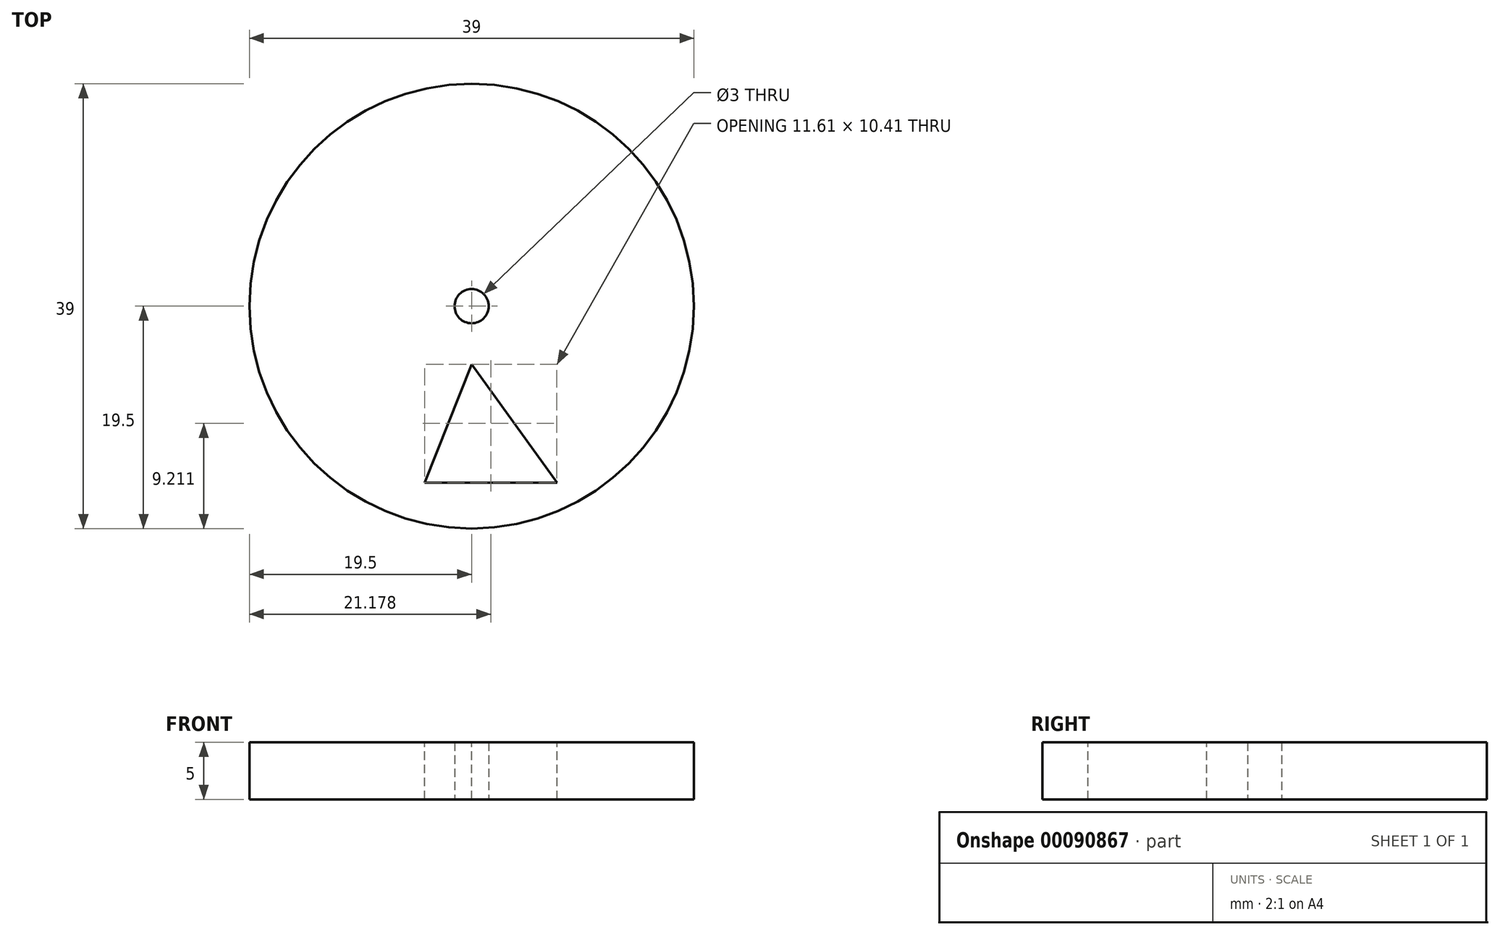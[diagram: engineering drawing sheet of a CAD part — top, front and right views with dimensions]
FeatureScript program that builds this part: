
annotation { "Feature Type Name" : "Feature", "Feature Type Description" : "" }
export const myFeature = defineFeature(function(context is Context, id is Id, definition is map)
    precondition{}
    {
        {
            var Q0;
            Q0=qCreatedBy(makeId("Top.planeOp"),FACE);
            var sketch = newSketch(context, id + "F0", { "sketchPlane" : qUnion([Q0])});
            skCircle(sketch, "E0", {"center": v(0, 0) * mm, "radius": 19.5 * mm});
            skCircle(sketch, "E1", {"center": v(0, 0) * mm, "radius": 1.5 * mm});
            skSolve(sketch);
        }
        {
            var Q0;
            Q0=makeQuery(id+"F0.imprint","IMPRINT",FACE,{"disambiguationData":[TD([[makeQuery(id+"F0.imprint","IMPRINT",EDGE,{"derivedFrom":sQuery(id+"F0.wireOp",EDGE,"E0")}),1.0]])]});
            extrude(context, id + "F1", {"entities" : qUnion([Q0]), "depth" : 5 * mm});
        }
        {
            var Q0;
            Q0=makeQuery(id+"F1.opExtrude","CAP_FACE",FACE,{"disambiguationData":[OSD([sQuery(id+"F0.wireOp",EDGE,"E0"),sQuery(id+"F0.wireOp",EDGE,"E1")])],"isStart":false});
            var sketch = newSketch(context, id + "F2", { "sketchPlane" : qUnion([Q0])});
            skPoint(sketch, "E2.middle", {"position": v(0, 0) * mm});
            skLineSegment(sketch, "E3", {"start": v(0, -5.09) * mm, "end": v(-4.13, -15.5) * mm});
            skLineSegment(sketch, "E4", {"start": v(-4.13, -15.5) * mm, "end": v(7.48, -15.5) * mm});
            skLineSegment(sketch, "E5", {"start": v(7.48, -15.5) * mm, "end": v(0, -5.09) * mm});
            skSolve(sketch);
        }
        {
            var Q0;
            Q0=makeQuery(id+"F2.imprint","IMPRINT",FACE,{"disambiguationData":[TD([[makeQuery(id+"F2.imprint","IMPRINT",EDGE,{"derivedFrom":sQuery(id+"F2.wireOp",EDGE,"E3")}),1.0]])]});
            extrude(context, id + "F3", {"entities" : qUnion([Q0]), "operationType" : NewBodyOperationType.REMOVE, "oppositeDirection" : true, "depth" : 5 * mm});
        }
    });
